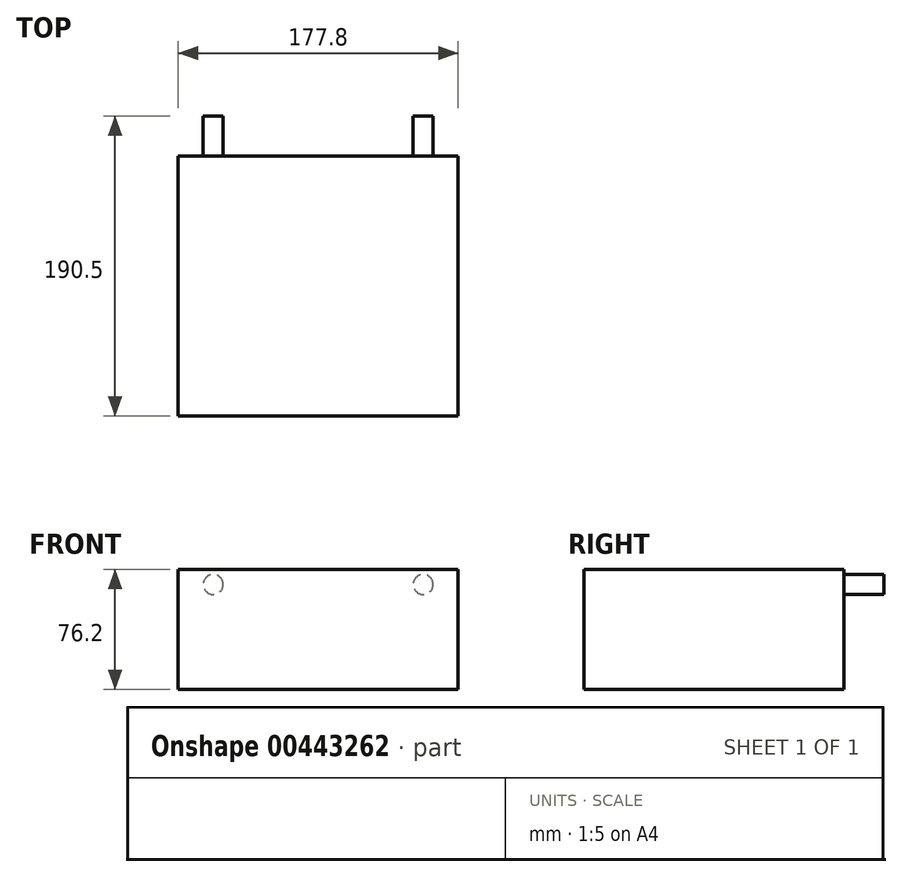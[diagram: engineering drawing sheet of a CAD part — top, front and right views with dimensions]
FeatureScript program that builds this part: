
annotation { "Feature Type Name" : "Feature", "Feature Type Description" : "" }
export const myFeature = defineFeature(function(context is Context, id is Id, definition is map)
    precondition{}
    {
        {
            var Q0;
            Q0=qCreatedBy(makeId("Top.planeOp"),FACE);
            var sketch = newSketch(context, id + "F0", { "sketchPlane" : qUnion([Q0])});
            skLineSegment(sketch, "E0.bottom", {"start": v(0, 0) * mm, "end": v(177.8, 0) * mm});
            skLineSegment(sketch, "E0.top", {"start": v(0, -165.1) * mm, "end": v(177.8, -165.1) * mm});
            skLineSegment(sketch, "E0.left", {"start": v(0, 0) * mm, "end": v(0, -165.1) * mm});
            skLineSegment(sketch, "E0.right", {"start": v(177.8, 0) * mm, "end": v(177.8, -165.1) * mm});
            skSolve(sketch);
        }
        {
            var Q0;
            Q0=makeQuery(id+"F0.imprint","IMPRINT",FACE,{"disambiguationData":[TD([[makeQuery(id+"F0.imprint","IMPRINT",EDGE,{"derivedFrom":sQuery(id+"F0.wireOp",EDGE,"E0.bottom")}),-1.0]])]});
            extrude(context, id + "F1", {"entities" : qUnion([Q0]), "depth" : 76.2 * mm});
        }
        {
            var Q0;
            Q0=makeQuery(id+"F1.opExtrude","SWEPT_FACE",FACE,{"disambiguationData":[OSD([sQuery(id+"F0.wireOp",EDGE,"E0.bottom")])]});
            var sketch = newSketch(context, id + "F2", { "sketchPlane" : qUnion([Q0])});
            skLineSegment(sketch, "E1", {"start": v(-177.8, 76.2) * mm, "end": v(-155.58, 76.2) * mm});
            skCircle(sketch, "E2", {"center": v(-155.58, 66.67) * mm, "radius": 6.35 * mm});
            skLineSegment(sketch, "E3", {"start": v(0, 76.2) * mm, "end": v(-22.23, 76.2) * mm});
            skCircle(sketch, "E4", {"center": v(-22.23, 66.67) * mm, "radius": 6.35 * mm});
            skSolve(sketch);
        }
        {
            var Q0;
            Q0=makeQuery(id+"F2.imprint","IMPRINT",FACE,{"disambiguationData":[TD([[makeQuery(id+"F2.imprint","IMPRINT",EDGE,{"derivedFrom":sQuery(id+"F2.wireOp",EDGE,"E2")}),1.0]])]});
            var Q1;
            Q1=makeQuery(id+"F2.imprint","IMPRINT",FACE,{"disambiguationData":[TD([[makeQuery(id+"F2.imprint","IMPRINT",EDGE,{"derivedFrom":sQuery(id+"F2.wireOp",EDGE,"E4")}),1.0]])]});
            var Q2;
            Q2=sQuery(id+"F2.wireOp",EDGE,"E4");
            extrude(context, id + "F3", {"entities" : qUnion([Q0, Q1]), "operationType" : NewBodyOperationType.ADD, "surfaceEntities" : qUnion([Q2]), "depth" : 25.4 * mm});
        }
    });
